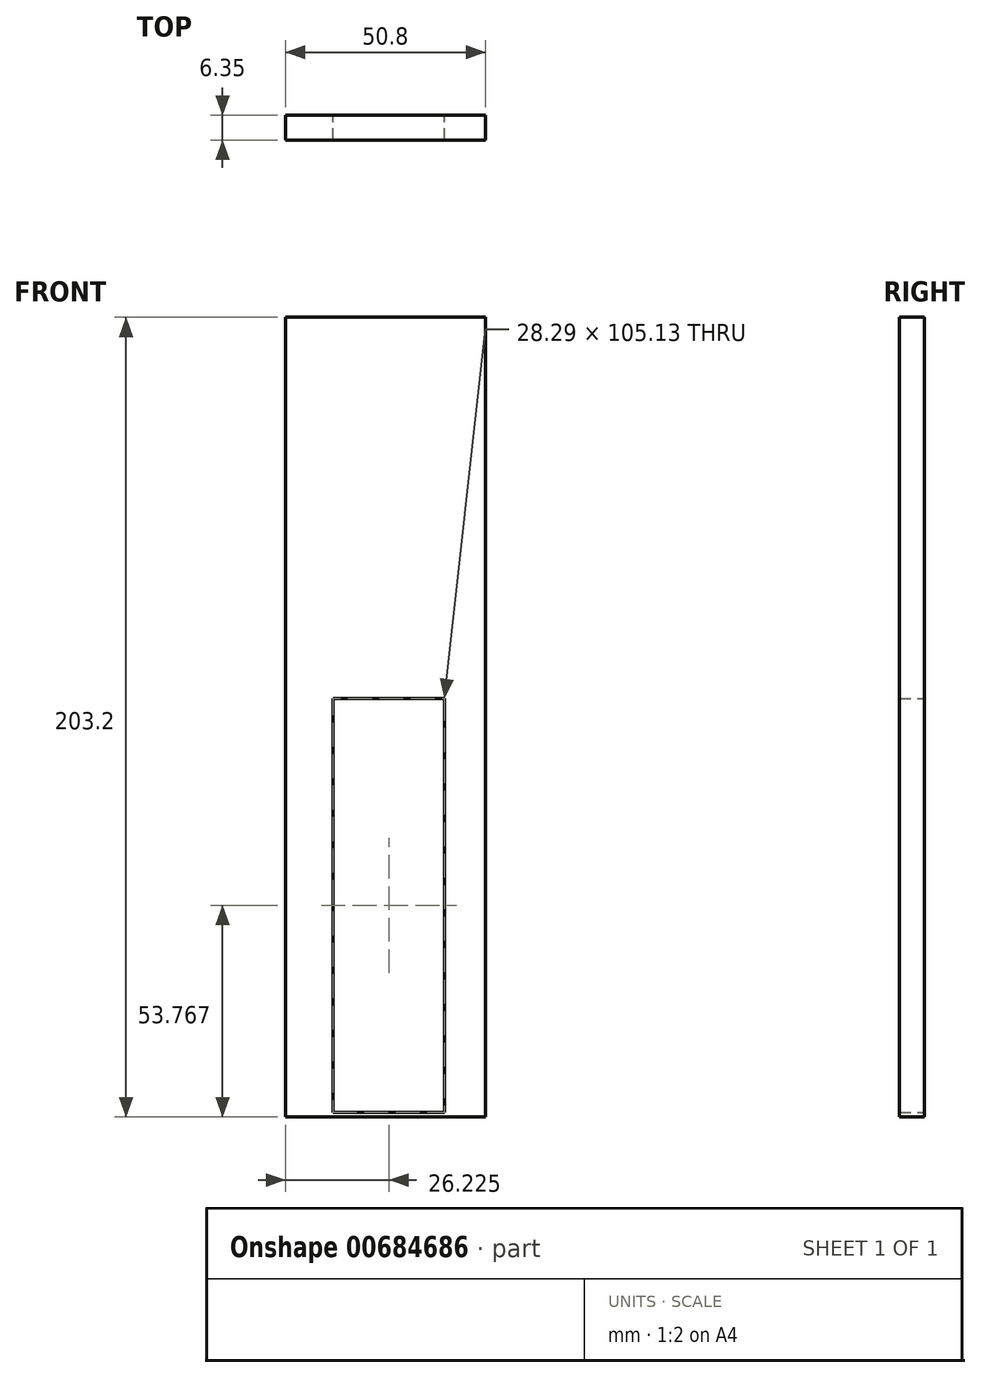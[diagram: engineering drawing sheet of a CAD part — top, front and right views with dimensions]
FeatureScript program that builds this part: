
annotation { "Feature Type Name" : "Feature", "Feature Type Description" : "" }
export const myFeature = defineFeature(function(context is Context, id is Id, definition is map)
    precondition{}
    {
        {
            var Q0;
            Q0=qCreatedBy(makeId("Front.planeOp"),FACE);
            var sketch = newSketch(context, id + "F0", { "sketchPlane" : qUnion([Q0])});
            skLineSegment(sketch, "E0.bottom", {"start": v(-36.48, 164.53) * mm, "end": v(14.32, 164.53) * mm});
            skLineSegment(sketch, "E0.top", {"start": v(-36.48, -38.67) * mm, "end": v(14.32, -38.67) * mm});
            skLineSegment(sketch, "E0.left", {"start": v(-36.48, 164.53) * mm, "end": v(-36.48, -38.67) * mm});
            skLineSegment(sketch, "E0.right", {"start": v(14.32, 164.53) * mm, "end": v(14.32, -38.67) * mm});
            skSolve(sketch);
        }
        {
            var Q0;
            Q0=qSketchRegion(id+"F0",true);
            extrude(context, id + "F1", {"entities" : qUnion([Q0]), "depth" : 6.35 * mm, "offsetDistance" : 25.4 * mm});
        }
        {
            var Q0;
            Q0=qCreatedBy(makeId("Front.planeOp"),FACE);
            var sketch = newSketch(context, id + "F2", { "sketchPlane" : qUnion([Q0])});
            skLineSegment(sketch, "E1.bottom", {"start": v(-24.4, -37.47) * mm, "end": v(3.9, -37.47) * mm});
            skLineSegment(sketch, "E1.top", {"start": v(-24.4, 67.66) * mm, "end": v(3.9, 67.66) * mm});
            skLineSegment(sketch, "E1.left", {"start": v(-24.4, -37.47) * mm, "end": v(-24.4, 67.66) * mm});
            skLineSegment(sketch, "E1.right", {"start": v(3.9, -37.47) * mm, "end": v(3.9, 67.66) * mm});
            skSolve(sketch);
        }
        {
            var Q0;
            Q0=qSketchRegion(id+"F2",true);
            extrude(context, id + "F3", {"entities" : qUnion([Q0]), "operationType" : NewBodyOperationType.REMOVE, "depth" : 25.4 * mm, "offsetDistance" : 25.4 * mm});
        }
    });
